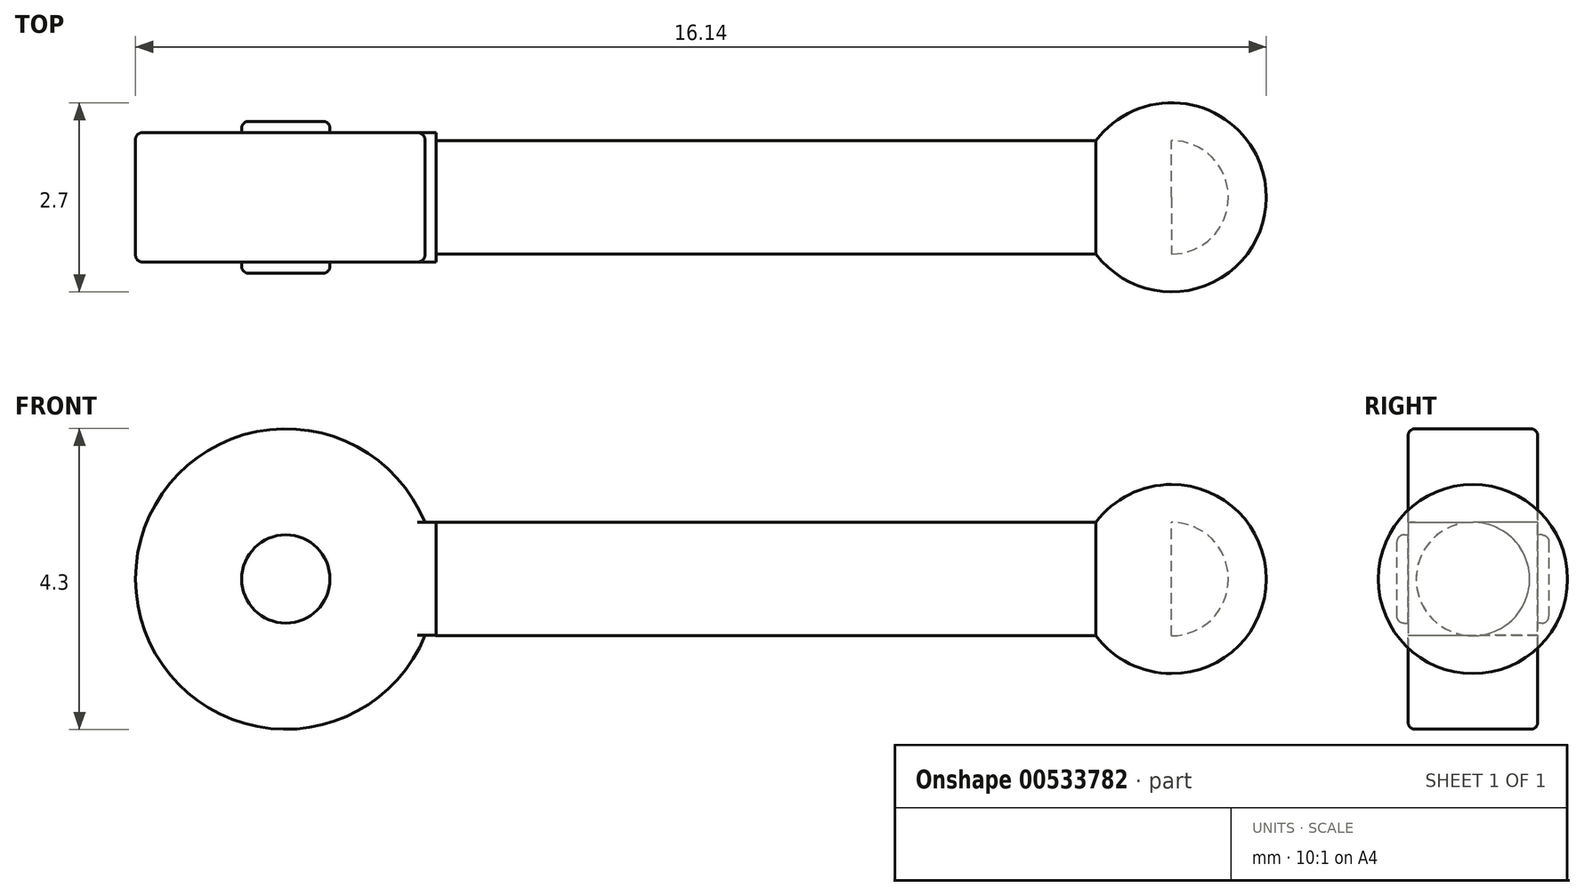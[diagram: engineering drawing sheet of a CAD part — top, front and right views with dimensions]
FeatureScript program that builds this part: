
annotation { "Feature Type Name" : "Feature", "Feature Type Description" : "" }
export const myFeature = defineFeature(function(context is Context, id is Id, definition is map)
    precondition{}
    {
        {
            var Q0;
            Q0=qCreatedBy(makeId("Right.planeOp"),FACE);
            var sketch = newSketch(context, id + "F0", { "sketchPlane" : qUnion([Q0])});
            skCircle(sketch, "E0", {"center": v(0, 0) * mm, "radius": 0.81 * mm});
            skSolve(sketch);
        }
        {
            var Q0;
            Q0=makeQuery(id+"F0.imprint","IMPRINT",FACE,{"disambiguationData":[TD([[makeQuery(id+"F0.imprint","IMPRINT",EDGE,{"derivedFrom":sQuery(id+"F0.wireOp",EDGE,"E0")}),1.0]])]});
            extrude(context, id + "F1", {"entities" : qUnion([Q0]), "depth" : 10.5 * mm});
        }
        {
            var Q0;
            Q0=qCreatedBy(makeId("Front.planeOp"),FACE);
            var sketch = newSketch(context, id + "F2", { "sketchPlane" : qUnion([Q0])});
            skArc(sketch, "E1", {"start": v(-0.16, 0.81) * mm, "mid": v(-4.29, 0) * mm, "end": v(-0.16, -0.8) * mm});
            skPoint(sketch, "E1.first.point", {"position": v(0, 0) * mm});
            skPoint(sketch, "E1.second.point", {"position": v(-4.3, 0) * mm});
            skPoint(sketch, "E1.third.point", {"position": v(-2.24, -2.14) * mm});
            skLineSegment(sketch, "E2", {"start": v(0, 0.81) * mm, "end": v(-0.16, 0.81) * mm});
            skLineSegment(sketch, "E3", {"start": v(0, -0.8) * mm, "end": v(-0.16, -0.8) * mm});
            skLineSegment(sketch, "E4", {"start": v(0, 0.81) * mm, "end": v(0, -0.8) * mm});
            skSolve(sketch);
        }
        {
            var Q0;
            Q0=makeQuery(id+"F2.imprint","IMPRINT",FACE,{"disambiguationData":[TD([[makeQuery(id+"F2.imprint","IMPRINT",EDGE,{"derivedFrom":sQuery(id+"F2.wireOp",EDGE,"E1")}),1.0]])]});
            extrude(context, id + "F3", {"entities" : qUnion([Q0]), "operationType" : NewBodyOperationType.ADD, "depth" : .925 * mm});
        }
        {
            var Q0;
            Q0=makeQuery(id+"F3.opExtrude","CAP_FACE",FACE,{"disambiguationData":[OSD([sQuery(id+"F2.wireOp",EDGE,"E1"),sQuery(id+"F2.wireOp",EDGE,"E2"),sQuery(id+"F2.wireOp",EDGE,"E3"),sQuery(id+"F2.wireOp",EDGE,"E4")])],"isStart":true});
            var sketch = newSketch(context, id + "F4", { "sketchPlane" : qUnion([Q0])});
            skArc(sketch, "E5", {"start": v(0.16, -0.8) * mm, "mid": v(4.29, 0) * mm, "end": v(0.16, 0.81) * mm});
            skLineSegment(sketch, "E6", {"start": v(0, -0.8) * mm, "end": v(0.16, -0.8) * mm});
            skLineSegment(sketch, "E7", {"start": v(0, 0.81) * mm, "end": v(0.16, 0.81) * mm});
            skLineSegment(sketch, "E8", {"start": v(0, 0.81) * mm, "end": v(0, -0.8) * mm});
            skSolve(sketch);
        }
        {
            var Q0;
            Q0=makeQuery(id+"F4.imprint","IMPRINT",FACE,{"disambiguationData":[TD([[makeQuery(id+"F4.imprint","IMPRINT",EDGE,{"derivedFrom":sQuery(id+"F4.wireOp",EDGE,"E5")}),-1.0]])]});
            extrude(context, id + "F5", {"entities" : qUnion([Q0]), "operationType" : NewBodyOperationType.ADD, "depth" : .925 * mm});
        }
        {
            var Q0;
            Q0=makeQuery(id+"F5.opExtrude","CAP_FACE",FACE,{"disambiguationData":[OSD([sQuery(id+"F4.wireOp",EDGE,"E5"),sQuery(id+"F4.wireOp",EDGE,"E6"),sQuery(id+"F4.wireOp",EDGE,"E7"),sQuery(id+"F4.wireOp",EDGE,"E8")])],"isStart":false});
            var sketch = newSketch(context, id + "F6", { "sketchPlane" : qUnion([Q0])});
            skCircle(sketch, "E9", {"center": v(2.15, 0) * mm, "radius": 0.63 * mm});
            skSolve(sketch);
        }
        {
            var Q0;
            Q0=makeQuery(id+"F3.opExtrude","CAP_FACE",FACE,{"disambiguationData":[OSD([sQuery(id+"F2.wireOp",EDGE,"E1"),sQuery(id+"F2.wireOp",EDGE,"E2"),sQuery(id+"F2.wireOp",EDGE,"E3"),sQuery(id+"F2.wireOp",EDGE,"E4")])],"isStart":false});
            var sketch = newSketch(context, id + "F7", { "sketchPlane" : qUnion([Q0])});
            skCircle(sketch, "E10", {"center": v(-2.15, 0) * mm, "radius": 0.63 * mm});
            skSolve(sketch);
        }
        {
            var Q0;
            Q0=makeQuery(id+"F7.imprint","IMPRINT",FACE,{"disambiguationData":[TD([[makeQuery(id+"F7.imprint","IMPRINT",EDGE,{"derivedFrom":sQuery(id+"F7.wireOp",EDGE,"E10")}),1.0]])]});
            extrude(context, id + "F8", {"entities" : qUnion([Q0]), "operationType" : NewBodyOperationType.ADD, "depth" : .16 * mm});
        }
        {
            var Q0;
            Q0=makeQuery(id+"F6.imprint","IMPRINT",FACE,{"disambiguationData":[TD([[makeQuery(id+"F6.imprint","IMPRINT",EDGE,{"derivedFrom":sQuery(id+"F6.wireOp",EDGE,"E9")}),1.0]])]});
            extrude(context, id + "F9", {"entities" : qUnion([Q0]), "operationType" : NewBodyOperationType.ADD, "depth" : .16 * mm});
        }
        {
            var Q0;
            Q0=makeQuery(id+"F9.opExtrude","CAP_FACE",FACE,{"disambiguationData":[OSD([sQuery(id+"F6.wireOp",EDGE,"E9")])],"isStart":false});
            var Q1;
            Q1=makeQuery(id+"F8.opExtrude","CAP_FACE",FACE,{"disambiguationData":[OSD([sQuery(id+"F7.wireOp",EDGE,"E10")])],"isStart":false});
            var Q2;
            Q2=makeQuery(id+"F3.opExtrude","CAP_EDGE",EDGE,{"disambiguationData":[OSD([sQuery(id+"F2.wireOp",EDGE,"E1")])],"isStart":false});
            var Q3;
            Q3=makeQuery(id+"F5.opExtrude","CAP_EDGE",EDGE,{"disambiguationData":[OSD([sQuery(id+"F4.wireOp",EDGE,"E5")])],"isStart":false});
            fillet(context, id + "F10", {"entities" : qUnion([Q0, Q1, Q2, Q3]), "radius" : .1 * mm, "tangentPropagation" : true, "allowEdgeOverflow" : false});
        }
        {
            var Q0;
            Q0=makeQuery(id+"F1.opExtrude","CAP_FACE",FACE,{"disambiguationData":[OSD([sQuery(id+"F0.wireOp",EDGE,"E0")])],"isStart":false});
            var sketch = newSketch(context, id + "F11", { "sketchPlane" : qUnion([Q0])});
            skArc(sketch, "E11", {"start": v(0, 1.35) * mm, "mid": v(-1.35, 0) * mm, "end": v(0, -1.35) * mm});
            skLineSegment(sketch, "E12", {"start": v(0, 1.35) * mm, "end": v(0, -1.35) * mm});
            skSolve(sketch);
        }
        {
            var Q0;
            {var subQ0=sQuery(id+"F11.wireOp",EDGE,"E11");Q0=makeQuery(id+"F11.imprint","IMPRINT",FACE,{"disambiguationData":[TD([[makeQuery(id+"F11.imprint","IMPRINT",EDGE,{"derivedFrom":subQ0}),1.0]])]});}
            var Q1;
            Q1=sQuery(id+"F11.wireOp",EDGE,"E12");
            revolve(context, id + "F12", {"operationType" : NewBodyOperationType.ADD, "entities" : qUnion([Q0]), "axis" : qUnion([Q1]), "revolveType" : RevolveType.FULL});
        }
    });
